# Revit family: Plymold-Essentials-Bolt_down_Seat_Post-
name_source: partatom
category: Furniture
units: mm (PartAtom-declared; Revit-internal decimal feet)

## family parameters
Always vertical = Yes
Cut with Voids When Loaded = No
OmniClass Number = 23.40.20.00
OmniClass Title = General Furniture and Specialties
Render Appearance Source = Family Geometry
Room Calculation Point = No
Shared = No
Work Plane-Based = No

## types (5) — shared parameters
Assembly Code = E2020200
BASE MATERIAL = PLY - Onyx Black Powdercoat
Brand = Seat Posts
Default Elevation = 0"
Depth = 9"
Keynote = 12500
Manufacturer = Plymold
POST MATERIAL = PLY - Onyx Black Powdercoat
Product Documentation Link = https://plymold.com
Revit Model Built By = https://www.servex-us.com
Sustainability = https://plymold.com
Type Comments = Chairs & Barstools
URL = https://plymold.com
Width = 9"
zero-valued in all types: Cost

## per-type parameters (varying)
| type | Description | Flat Base | Foot Rest | Height |
| 56601 | Bolt-down Seat Post – Dining Height - 9”W x 9”D x 18”H | No | No | 18" |
| 56601-01 | Flat Base Bolt-down Seat Post – Dining Height - 9”W x 9”D x 18”H | Yes | No | 18" |
| 56701 | Bolt-down Seat Post – Bar Height - 9”W x 9”D x 30”H | No | No | 30" |
| 56701-01 | Flat Base Bolt-down Seat Post – Bar Height Footrest - 9”W x 9”D x 30”H | Yes | Yes | 30" |
| 56701-02 | Flat Base Bolt-down Seat Post – Bar Height - 9”W x 9”D x 30”H | Yes | No | 30" |

note: column(s) folded — value = type name in every type: Model

## geometry (parser evidence)
native form markers: Sweep x4
no freeform markers — native parametric forms only
